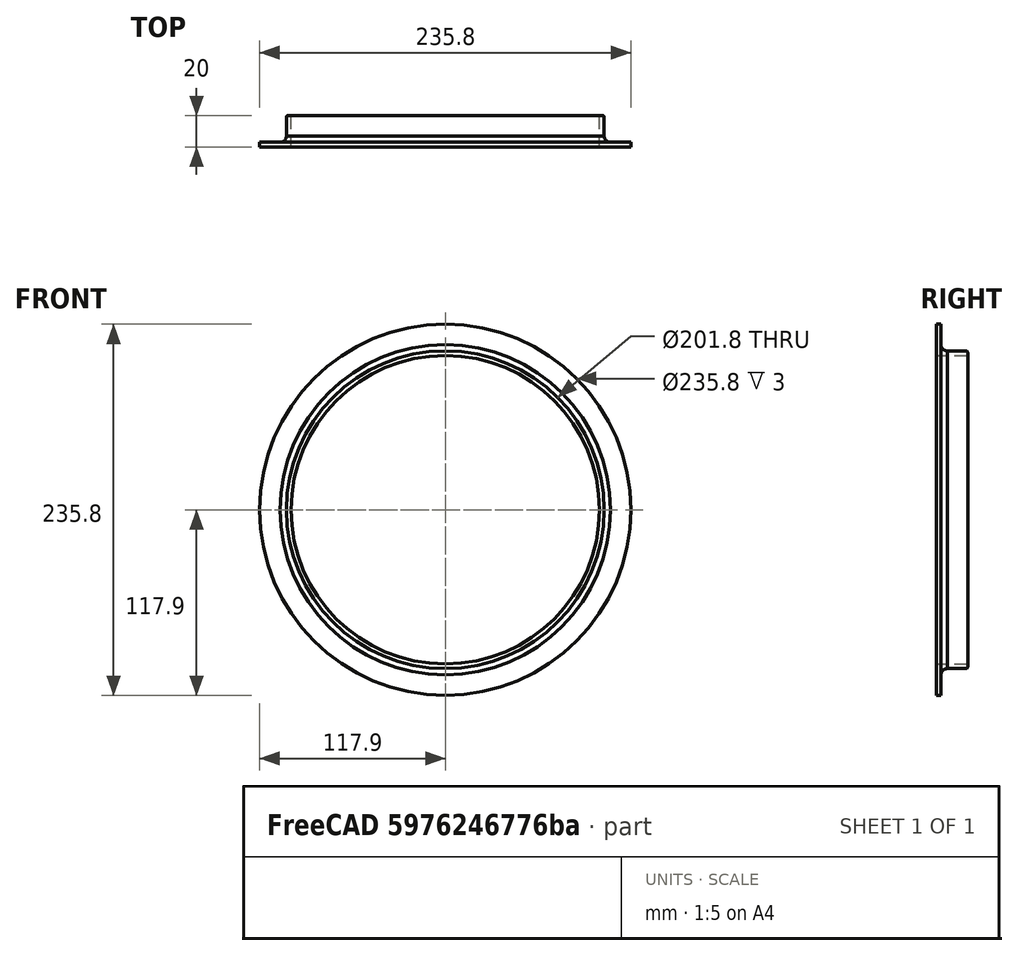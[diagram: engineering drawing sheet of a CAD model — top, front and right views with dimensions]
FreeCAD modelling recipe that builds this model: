
FCSTD DOCUMENT  (FreeCAD 0.18R16110 (Git))
Label: 7inducking
License: All rights reserved
LicenseURL: http://en.wikipedia.org/wiki/All_rights_reserved
objects: Sketcher::SketchObject×1, Part::Revolution×1, Part::Fillet×1
note: 3 computed .brp shape members not serialized (recipe doc carries the construction recipe); baked Part::Feature solids carry a one-line shape summary decoded from their .brp

FEATURE [Sketcher::SketchObject] Sketch
  sketch-geometry (7):
    g0: LineSegment StartX=97.9 StartY=0 StartZ=0 EndX=97.9 EndY=20 EndZ=0
    g1: LineSegment StartX=97.9 StartY=20 StartZ=0 EndX=100.9 EndY=20 EndZ=0
    g2: LineSegment StartX=97.9 StartY=0 StartZ=0 EndX=117.9 EndY=0 EndZ=0
    g3: LineSegment StartX=117.9 StartY=0 StartZ=0 EndX=117.9 EndY=3 EndZ=0
    g4: LineSegment StartX=117.9 StartY=3 StartZ=0 EndX=104.9 EndY=3 EndZ=0
    g5: LineSegment StartX=100.9 StartY=20 StartZ=0 EndX=100.9 EndY=7 EndZ=0
    g6: ArcOfCircle CenterX=104.989 CenterY=7.08903 CenterZ=0 NormalX=0 NormalY=0 NormalZ=1 AngleXU=0 Radius=4.09 StartAngle=3.16336 EndAngle=4.69062
  constraints (22):
    c: PointOnObject(g0,g-1)
    c: Vertical(g0)
    c: DistanceX(g0) = 97.9
    c: DistanceY(g0) = 20
    c: Coincident(g1,g0)
    c: Horizontal(g1)
    c: DistanceX(g1,g1) = 3
    c: Coincident(g0,g2)
    c: PointOnObject(g2,g-1)
    c: Coincident(g2,g3)
    c: Vertical(g3)
    c: Coincident(g3,g4)
    c: Coincident(g5,g1)
    c: Vertical(g5)
    c: Coincident(g6,g5)
    c: Coincident(g6,g4)
    c: Horizontal(g4)
    c: DistanceY(g3,g3) = 3
    c: DistanceX(g4,g4) = 13
    c: DistanceY(g5,g5) = 13
    c: Radius(g6) = 4.09
    c: DistanceX(g2,g2) = 20
FEATURE [Part::Revolution] Revolve
  Angle = 360
  Axis = (0,1,0)
  Base = (0,0,0)
  FaceMakerClass = Part::FaceMakerBullseye
  Solid = false
  Source = -> Sketch
  Symmetric = false
FEATURE [Part::Fillet] Fillet
  Base = -> Revolve
  Edges = 1 edges r=1: [Edge4]
